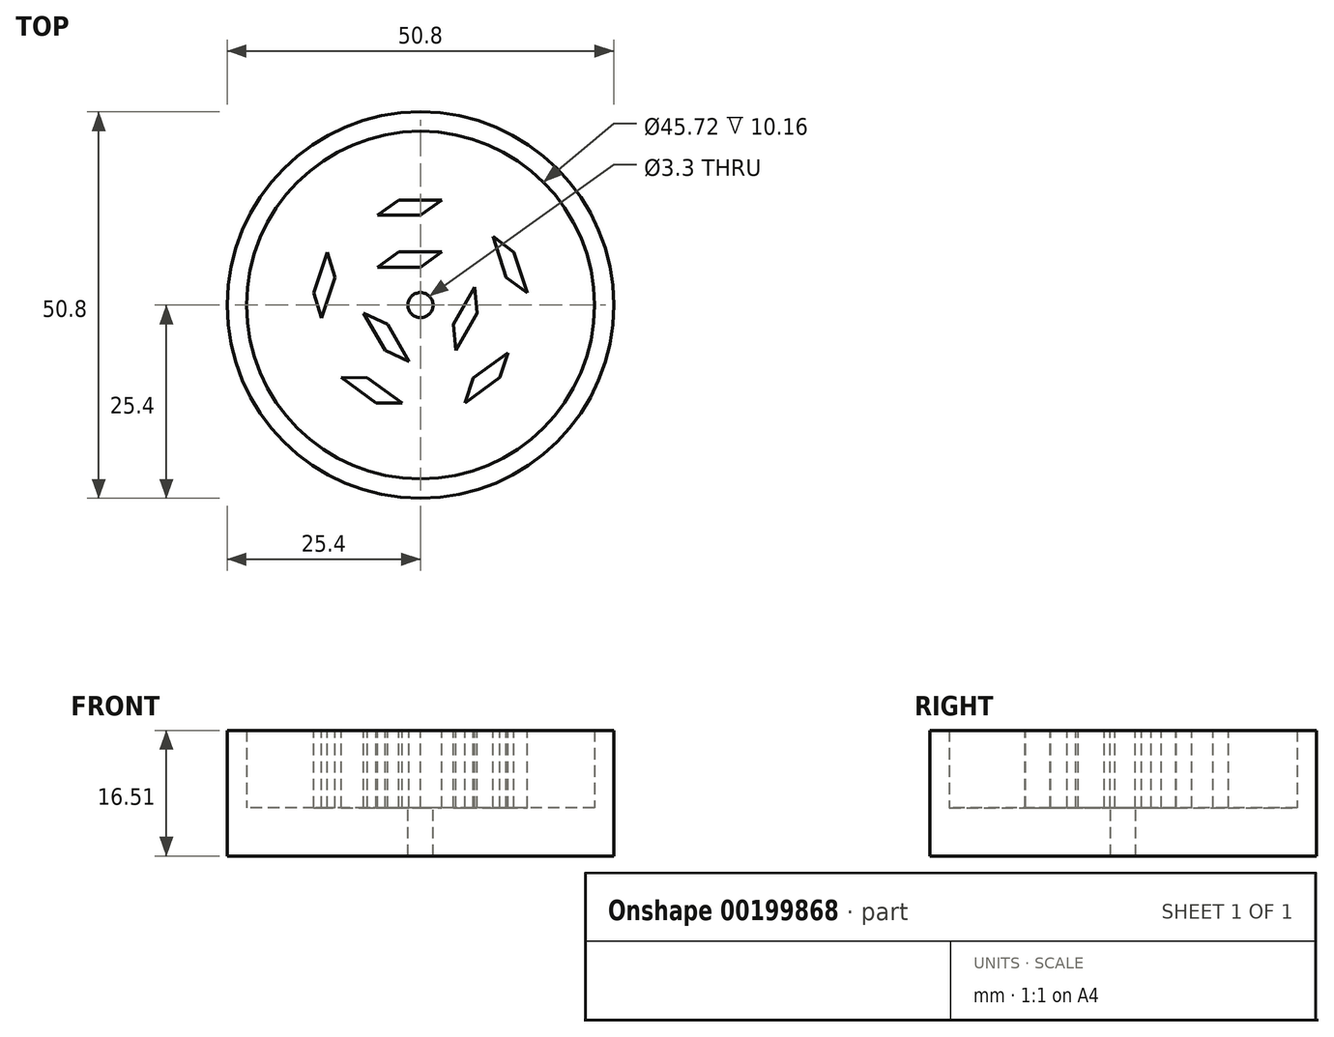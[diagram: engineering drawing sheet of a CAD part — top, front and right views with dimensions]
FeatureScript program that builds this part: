
annotation { "Feature Type Name" : "Feature", "Feature Type Description" : "" }
export const myFeature = defineFeature(function(context is Context, id is Id, definition is map)
    precondition{}
    {
        {
            var Q0;
            Q0=qCreatedBy(makeId("Top.planeOp"),FACE);
            var sketch = newSketch(context, id + "F0", { "sketchPlane" : qUnion([Q0])});
            skCircle(sketch, "E0", {"center": v(0, 0) * mm, "radius": 25.4 * mm});
            skSolve(sketch);
        }
        {
            var Q0;
            Q0=makeQuery(id+"F0.imprint","IMPRINT",FACE,{"disambiguationData":[TD([[makeQuery(id+"F0.imprint","IMPRINT",EDGE,{"derivedFrom":sQuery(id+"F0.wireOp",EDGE,"E0")}),1.0]])]});
            extrude(context, id + "F1", {"entities" : qUnion([Q0]), "depth" : 6.35 * mm});
        }
        {
            var Q0;
            Q0=makeQuery(id+"F1.opExtrude","CAP_FACE",FACE,{"disambiguationData":[OSD([sQuery(id+"F0.wireOp",EDGE,"E0")])],"isStart":false});
            var sketch = newSketch(context, id + "F2", { "sketchPlane" : qUnion([Q0])});
            skCircle(sketch, "E1", {"center": v(0, 0) * mm, "radius": 22.86 * mm});
            skSolve(sketch);
        }
        {
            var Q0;
            Q0=makeQuery(id+"F2.imprint","IMPRINT",FACE,{"disambiguationData":[TD([[makeQuery(id+"F2.imprint","IMPRINT",EDGE,{"derivedFrom":sQuery(id+"F2.wireOp",EDGE,"E1")}),1.0]])]});
            extrude(context, id + "F3", {"entities" : qUnion([Q0]), "operationType" : NewBodyOperationType.ADD, "depth" : 10.16 * mm});
        }
        {
            var Q0;
            Q0=makeQuery(id+"F3.opExtrude","CAP_FACE",FACE,{"disambiguationData":[OSD([sQuery(id+"F2.wireOp",EDGE,"E1")])],"isStart":false});
            var sketch = newSketch(context, id + "F4", { "sketchPlane" : qUnion([Q0])});
            skCircle(sketch, "E2", {"center": v(0, 0) * mm, "radius": 20.32 * mm});
            skCircle(sketch, "E3", {"center": v(0, 0) * mm, "radius": 1.65 * mm, "construction": true});
            skCircle(sketch, "E4.cCircle", {"center": v(0, 0) * mm, "radius": 1.53 * mm, "construction": true});
            skCircle(sketch, "E5", {"center": v(0, 0) * mm, "radius": 5 * mm, "construction": true});
            skCircle(sketch, "E6.0", {"center": v(0, 0) * mm, "radius": 7.53 * mm, "construction": true});
            skLineSegment(sketch, "E7", {"start": v(0, 5) * mm, "end": v(2.82, 6.98) * mm});
            skLineSegment(sketch, "E8", {"start": v(2.82, 6.98) * mm, "end": v(-2.82, 6.98) * mm});
            skLineSegment(sketch, "E9", {"start": v(-2.82, 6.98) * mm, "end": v(-5.64, 5) * mm});
            skLineSegment(sketch, "E10", {"start": v(-5.64, 5) * mm, "end": v(0, 5) * mm});
            skCircle(sketch, "E11", {"center": v(0, 0) * mm, "radius": 8.38 * mm, "construction": true});
            skCircle(sketch, "E12.0", {"center": v(0, 0) * mm, "radius": 10.92 * mm, "construction": true});
            skLineSegment(sketch, "E13", {"start": v(0, 8.56) * mm, "end": v(2.82, 10.55) * mm, "construction": true});
            skLineSegment(sketch, "E14", {"start": v(2.82, 10.55) * mm, "end": v(-2.82, 10.55) * mm, "construction": true});
            skLineSegment(sketch, "E15", {"start": v(-2.82, 10.55) * mm, "end": v(-5.64, 8.56) * mm, "construction": true});
            skLineSegment(sketch, "E16", {"start": v(-5.64, 8.56) * mm, "end": v(0, 8.56) * mm, "construction": true});
            skCircle(sketch, "E17", {"center": v(0, 0) * mm, "radius": 11.57 * mm, "construction": true});
            skCircle(sketch, "E18.0", {"center": v(0, 0) * mm, "radius": 14.1 * mm, "construction": true});
            skLineSegment(sketch, "E19", {"start": v(0, 11.83) * mm, "end": v(2.82, 13.82) * mm});
            skLineSegment(sketch, "E20", {"start": v(2.82, 13.82) * mm, "end": v(-2.82, 13.82) * mm});
            skLineSegment(sketch, "E21", {"start": v(-2.82, 13.82) * mm, "end": v(-5.64, 11.83) * mm});
            skLineSegment(sketch, "E22", {"start": v(-5.64, 11.83) * mm, "end": v(0, 11.83) * mm});
            skCircle(sketch, "E23", {"center": v(0, 0) * mm, "radius": 14.85 * mm});
            skCircle(sketch, "E24.0", {"center": v(0, 0) * mm, "radius": 17.39 * mm});
            skLineSegment(sketch, "E25", {"start": v(0, 15.17) * mm, "end": v(2.82, 17.16) * mm});
            skLineSegment(sketch, "E26", {"start": v(2.82, 17.16) * mm, "end": v(-2.82, 17.16) * mm});
            skLineSegment(sketch, "E27", {"start": v(-2.82, 17.16) * mm, "end": v(-5.64, 15.17) * mm, "construction": true});
            skLineSegment(sketch, "E28", {"start": v(-5.64, 15.17) * mm, "end": v(0, 15.17) * mm, "construction": true});
            skPoint(sketch, "E29", {"position": v(0, 17.16) * mm});
            skLineSegment(sketch, "E30", {"start": v(0, 0) * mm, "end": v(0, 26.22) * mm, "construction": true});
            skCircle(sketch, "E31.cCircle", {"center": v(0, 0) * mm, "radius": 1.7 * mm, "construction": true});
            skLineSegment(sketch, "E31.0", {"start": v(-2.95, -1.7) * mm, "end": v(0, 3.4) * mm, "construction": true});
            skLineSegment(sketch, "E31.1", {"start": v(0, 3.4) * mm, "end": v(2.95, -1.7) * mm, "construction": true});
            skLineSegment(sketch, "E31.2", {"start": v(2.95, -1.7) * mm, "end": v(-2.95, -1.7) * mm, "construction": true});
            skPoint(sketch, "E31.0.midPoint", {"position": v(-1.47, 0.85) * mm});
            skLineSegment(sketch, "E32.1.0", {"start": v(-11.86, 9.46) * mm, "end": v(-11.66, 12.9) * mm, "construction": true});
            skLineSegment(sketch, "E32.1.1", {"start": v(-15.37, 5.05) * mm, "end": v(-11.86, 9.46) * mm, "construction": true});
            skLineSegment(sketch, "E32.1.2", {"start": v(-15.17, 8.5) * mm, "end": v(-15.37, 5.05) * mm, "construction": true});
            skLineSegment(sketch, "E32.1.3", {"start": v(-11.66, 12.9) * mm, "end": v(-15.17, 8.5) * mm, "construction": true});
            skLineSegment(sketch, "E32.2.0", {"start": v(-14.79, -3.37) * mm, "end": v(-17.36, -1.07) * mm, "construction": true});
            skLineSegment(sketch, "E32.2.1", {"start": v(-13.53, -8.87) * mm, "end": v(-14.79, -3.37) * mm, "construction": true});
            skLineSegment(sketch, "E32.2.2", {"start": v(-16.1, -6.57) * mm, "end": v(-13.53, -8.87) * mm, "construction": true});
            skLineSegment(sketch, "E32.2.3", {"start": v(-17.36, -1.07) * mm, "end": v(-16.1, -6.57) * mm, "construction": true});
            skLineSegment(sketch, "E32.3.0", {"start": v(-6.58, -13.66) * mm, "end": v(-9.99, -14.24) * mm, "construction": true});
            skLineSegment(sketch, "E32.3.1", {"start": v(-1.5, -16.11) * mm, "end": v(-6.58, -13.66) * mm, "construction": true});
            skLineSegment(sketch, "E32.3.2", {"start": v(-4.9, -16.68) * mm, "end": v(-1.5, -16.11) * mm, "construction": true});
            skLineSegment(sketch, "E32.3.3", {"start": v(-9.99, -14.24) * mm, "end": v(-4.9, -16.68) * mm, "construction": true});
            skLineSegment(sketch, "E32.4.0", {"start": v(6.58, -13.66) * mm, "end": v(4.9, -16.68) * mm, "construction": true});
            skLineSegment(sketch, "E32.4.1", {"start": v(11.66, -11.22) * mm, "end": v(6.58, -13.66) * mm, "construction": true});
            skLineSegment(sketch, "E32.4.2", {"start": v(9.99, -14.24) * mm, "end": v(11.66, -11.22) * mm, "construction": true});
            skLineSegment(sketch, "E32.4.3", {"start": v(4.9, -16.68) * mm, "end": v(9.99, -14.24) * mm, "construction": true});
            skLineSegment(sketch, "E32.5.0", {"start": v(14.79, -3.37) * mm, "end": v(16.1, -6.57) * mm, "construction": true});
            skLineSegment(sketch, "E32.5.1", {"start": v(16.04, 2.12) * mm, "end": v(14.79, -3.37) * mm, "construction": true});
            skLineSegment(sketch, "E32.5.2", {"start": v(17.36, -1.07) * mm, "end": v(16.04, 2.12) * mm, "construction": true});
            skLineSegment(sketch, "E32.5.3", {"start": v(16.1, -6.57) * mm, "end": v(17.36, -1.07) * mm, "construction": true});
            skLineSegment(sketch, "E32.6.0", {"start": v(11.86, 9.46) * mm, "end": v(15.17, 8.5) * mm, "construction": true});
            skLineSegment(sketch, "E32.6.1", {"start": v(8.34, 13.87) * mm, "end": v(11.86, 9.46) * mm, "construction": true});
            skLineSegment(sketch, "E32.6.2", {"start": v(11.66, 12.9) * mm, "end": v(8.34, 13.87) * mm, "construction": true});
            skLineSegment(sketch, "E32.6.3", {"start": v(15.17, 8.5) * mm, "end": v(11.66, 12.9) * mm, "construction": true});
            skLineSegment(sketch, "E33.1.0", {"start": v(-8.56, 0) * mm, "end": v(-10.55, 2.82) * mm, "construction": true});
            skLineSegment(sketch, "E33.1.1", {"start": v(-10.55, 2.82) * mm, "end": v(-10.55, -2.82) * mm, "construction": true});
            skLineSegment(sketch, "E33.1.2", {"start": v(-8.56, -5.64) * mm, "end": v(-8.56, 0) * mm, "construction": true});
            skLineSegment(sketch, "E33.1.3", {"start": v(-10.55, -2.82) * mm, "end": v(-8.56, -5.64) * mm, "construction": true});
            skLineSegment(sketch, "E33.2.0", {"start": v(0, -8.56) * mm, "end": v(-2.82, -10.55) * mm, "construction": true});
            skLineSegment(sketch, "E33.2.1", {"start": v(-2.82, -10.55) * mm, "end": v(2.82, -10.55) * mm, "construction": true});
            skLineSegment(sketch, "E33.2.2", {"start": v(5.64, -8.56) * mm, "end": v(0, -8.56) * mm, "construction": true});
            skLineSegment(sketch, "E33.2.3", {"start": v(2.82, -10.55) * mm, "end": v(5.64, -8.56) * mm, "construction": true});
            skLineSegment(sketch, "E34.1.3.0", {"start": v(8.56, 0) * mm, "end": v(10.55, -2.82) * mm, "construction": true});
            skLineSegment(sketch, "E34.3.3.0", {"start": v(10.55, -2.82) * mm, "end": v(10.55, 2.82) * mm, "construction": true});
            skLineSegment(sketch, "E34.6.3.0", {"start": v(8.56, 5.64) * mm, "end": v(8.56, 0) * mm, "construction": true});
            skLineSegment(sketch, "E34.9.3.0", {"start": v(10.55, 2.82) * mm, "end": v(8.56, 5.64) * mm, "construction": true});
            skCircle(sketch, "E35", {"center": v(0, 0) * mm, "radius": 22.86 * mm});
            skLineSegment(sketch, "E36.1.0", {"start": v(-4.32, -2.5) * mm, "end": v(-7.46, -1.05) * mm});
            skLineSegment(sketch, "E36.1.1", {"start": v(-7.46, -1.05) * mm, "end": v(-4.64, -5.93) * mm});
            skLineSegment(sketch, "E36.1.2", {"start": v(-1.5, -7.38) * mm, "end": v(-4.32, -2.5) * mm});
            skLineSegment(sketch, "E36.1.3", {"start": v(-4.64, -5.93) * mm, "end": v(-1.5, -7.38) * mm});
            skLineSegment(sketch, "E36.2.0", {"start": v(4.32, -2.5) * mm, "end": v(4.64, -5.93) * mm});
            skLineSegment(sketch, "E36.2.1", {"start": v(4.64, -5.93) * mm, "end": v(7.46, -1.05) * mm});
            skLineSegment(sketch, "E36.2.2", {"start": v(7.14, 2.39) * mm, "end": v(4.32, -2.5) * mm});
            skLineSegment(sketch, "E36.2.3", {"start": v(7.46, -1.05) * mm, "end": v(7.14, 2.39) * mm});
            skLineSegment(sketch, "E37.1.0", {"start": v(-11.25, 3.66) * mm, "end": v(-12.27, 6.95) * mm});
            skLineSegment(sketch, "E37.1.1", {"start": v(-12.27, 6.95) * mm, "end": v(-14.02, 1.59) * mm});
            skLineSegment(sketch, "E37.1.2", {"start": v(-13, -1.7) * mm, "end": v(-11.25, 3.66) * mm});
            skLineSegment(sketch, "E37.1.3", {"start": v(-14.02, 1.59) * mm, "end": v(-13, -1.7) * mm});
            skLineSegment(sketch, "E37.2.0", {"start": v(-6.95, -9.57) * mm, "end": v(-10.4, -9.52) * mm});
            skLineSegment(sketch, "E37.2.1", {"start": v(-10.4, -9.52) * mm, "end": v(-5.84, -12.84) * mm});
            skLineSegment(sketch, "E37.2.2", {"start": v(-2.4, -12.89) * mm, "end": v(-6.95, -9.57) * mm});
            skLineSegment(sketch, "E37.2.3", {"start": v(-5.84, -12.84) * mm, "end": v(-2.4, -12.89) * mm});
            skLineSegment(sketch, "E37.3.0", {"start": v(6.95, -9.57) * mm, "end": v(5.84, -12.84) * mm});
            skLineSegment(sketch, "E37.3.1", {"start": v(5.84, -12.84) * mm, "end": v(10.4, -9.52) * mm});
            skLineSegment(sketch, "E37.3.2", {"start": v(11.52, -6.26) * mm, "end": v(6.95, -9.57) * mm});
            skLineSegment(sketch, "E37.3.3", {"start": v(10.4, -9.52) * mm, "end": v(11.52, -6.26) * mm});
            skLineSegment(sketch, "E37.4.0", {"start": v(11.25, 3.66) * mm, "end": v(14.02, 1.59) * mm});
            skLineSegment(sketch, "E37.4.1", {"start": v(14.02, 1.59) * mm, "end": v(12.27, 6.95) * mm});
            skLineSegment(sketch, "E37.4.2", {"start": v(9.5, 9.02) * mm, "end": v(11.25, 3.66) * mm});
            skLineSegment(sketch, "E37.4.3", {"start": v(12.27, 6.95) * mm, "end": v(9.5, 9.02) * mm});
            skSolve(sketch);
        }
        {
            var Q0;
            Q0=makeQuery(id+"F4.imprint","IMPRINT",FACE,{"disambiguationData":[TD([[makeQuery(id+"F4.imprint","IMPRINT",EDGE,{"derivedFrom":sQuery(id+"F4.wireOp",EDGE,"E2")}),-1.0]])]});
            var Q1;
            Q1=makeQuery(id+"F4.imprint","IMPRINT",FACE,{"disambiguationData":[TD([[makeQuery(id+"F4.imprint","IMPRINT",EDGE,{"derivedFrom":sQuery(id+"F4.wireOp",EDGE,"E23")}),-1.0]])]});
            var Q2;
            Q2=makeQuery(id+"F4.imprint","IMPRINT",FACE,{"disambiguationData":[TD([[makeQuery(id+"F4.imprint","IMPRINT",EDGE,{"derivedFrom":sQuery(id+"F4.wireOp",EDGE,"E7")}),-1.0]])]});
            var Q3;
            Q3=makeQuery(id+"F4.imprint","IMPRINT",FACE,{"disambiguationData":[TD([[makeQuery(id+"F4.imprint","IMPRINT",EDGE,{"derivedFrom":sQuery(id+"F4.wireOp",EDGE,"E2")}),1.0]])]});
            var Q4;
            {var subQ0=sQuery(id+"F4.wireOp",EDGE,"E26");Q4=makeQuery(id+"F4.imprint","IMPRINT",FACE,{"disambiguationData":[TD([[makeQuery(id+"F4.imprint","IMPRINT",EDGE,{"derivedFrom":subQ0}),-1.0]])]});}
            extrude(context, id + "F5", {"entities" : qUnion([Q0, Q1, Q2, Q3, Q4]), "operationType" : NewBodyOperationType.REMOVE, "oppositeDirection" : true, "depth" : 10.16 * mm});
        }
        {
            var Q0;
            Q0=makeQuery(id+"F5.boolean.opBoolean","MERGE",FACE,{"derivedFrom":[makeQuery(id+"F1.opExtrude","CAP_FACE",FACE,{"disambiguationData":[OSD([sQuery(id+"F0.wireOp",EDGE,"E0")])],"isStart":false}),makeQuery(id+"F5.opExtrude","CAP_FACE",FACE,{"disambiguationData":[OSD([sQuery(id+"F4.wireOp",EDGE,"E7"),sQuery(id+"F4.wireOp",EDGE,"E8"),sQuery(id+"F4.wireOp",EDGE,"E9"),sQuery(id+"F4.wireOp",EDGE,"E10"),sQuery(id+"F4.wireOp",EDGE,"E19"),sQuery(id+"F4.wireOp",EDGE,"E20"),sQuery(id+"F4.wireOp",EDGE,"E21"),sQuery(id+"F4.wireOp",EDGE,"E22"),sQuery(id+"F4.wireOp",EDGE,"E35"),sQuery(id+"F4.wireOp",EDGE,"E36.1.0"),sQuery(id+"F4.wireOp",EDGE,"E36.1.1"),sQuery(id+"F4.wireOp",EDGE,"E36.1.2"),sQuery(id+"F4.wireOp",EDGE,"E36.1.3"),sQuery(id+"F4.wireOp",EDGE,"E36.2.0"),sQuery(id+"F4.wireOp",EDGE,"E36.2.1"),sQuery(id+"F4.wireOp",EDGE,"E36.2.2"),sQuery(id+"F4.wireOp",EDGE,"E36.2.3"),sQuery(id+"F4.wireOp",EDGE,"E37.1.0"),sQuery(id+"F4.wireOp",EDGE,"E37.1.1"),sQuery(id+"F4.wireOp",EDGE,"E37.1.2"),sQuery(id+"F4.wireOp",EDGE,"E37.1.3"),sQuery(id+"F4.wireOp",EDGE,"E37.2.0"),sQuery(id+"F4.wireOp",EDGE,"E37.2.1"),sQuery(id+"F4.wireOp",EDGE,"E37.2.2"),sQuery(id+"F4.wireOp",EDGE,"E37.2.3"),sQuery(id+"F4.wireOp",EDGE,"E37.3.0"),sQuery(id+"F4.wireOp",EDGE,"E37.3.1"),sQuery(id+"F4.wireOp",EDGE,"E37.3.2"),sQuery(id+"F4.wireOp",EDGE,"E37.3.3"),sQuery(id+"F4.wireOp",EDGE,"E37.4.0"),sQuery(id+"F4.wireOp",EDGE,"E37.4.1"),sQuery(id+"F4.wireOp",EDGE,"E37.4.2"),sQuery(id+"F4.wireOp",EDGE,"E37.4.3")])],"isStart":false})]});
            var sketch = newSketch(context, id + "F6", { "sketchPlane" : qUnion([Q0])});
            skCircle(sketch, "E38.0", {"center": v(0, 0) * mm, "radius": 22.86 * mm});
            skCircle(sketch, "E39", {"center": v(0, 0) * mm, "radius": 25.4 * mm});
            skSolve(sketch);
        }
        {
            var Q0;
            Q0=makeQuery(id+"F6.imprint","IMPRINT",FACE,{"disambiguationData":[TD([[makeQuery(id+"F6.imprint","IMPRINT",EDGE,{"derivedFrom":sQuery(id+"F6.wireOp",EDGE,"E38.0")}),-1.0]])]});
            extrude(context, id + "F7", {"entities" : qUnion([Q0]), "operationType" : NewBodyOperationType.ADD, "depth" : 10.16 * mm});
        }
        {
            var Q0;
            Q0=makeQuery(id+"F5.boolean.opBoolean","MERGE",FACE,{"derivedFrom":[makeQuery(id+"F1.opExtrude","CAP_FACE",FACE,{"disambiguationData":[OSD([sQuery(id+"F0.wireOp",EDGE,"E0")])],"isStart":false}),makeQuery(id+"F5.opExtrude","CAP_FACE",FACE,{"disambiguationData":[OSD([sQuery(id+"F4.wireOp",EDGE,"E7"),sQuery(id+"F4.wireOp",EDGE,"E8"),sQuery(id+"F4.wireOp",EDGE,"E9"),sQuery(id+"F4.wireOp",EDGE,"E10"),sQuery(id+"F4.wireOp",EDGE,"E19"),sQuery(id+"F4.wireOp",EDGE,"E20"),sQuery(id+"F4.wireOp",EDGE,"E21"),sQuery(id+"F4.wireOp",EDGE,"E22"),sQuery(id+"F4.wireOp",EDGE,"E35"),sQuery(id+"F4.wireOp",EDGE,"E36.1.0"),sQuery(id+"F4.wireOp",EDGE,"E36.1.1"),sQuery(id+"F4.wireOp",EDGE,"E36.1.2"),sQuery(id+"F4.wireOp",EDGE,"E36.1.3"),sQuery(id+"F4.wireOp",EDGE,"E36.2.0"),sQuery(id+"F4.wireOp",EDGE,"E36.2.1"),sQuery(id+"F4.wireOp",EDGE,"E36.2.2"),sQuery(id+"F4.wireOp",EDGE,"E36.2.3"),sQuery(id+"F4.wireOp",EDGE,"E37.1.0"),sQuery(id+"F4.wireOp",EDGE,"E37.1.1"),sQuery(id+"F4.wireOp",EDGE,"E37.1.2"),sQuery(id+"F4.wireOp",EDGE,"E37.1.3"),sQuery(id+"F4.wireOp",EDGE,"E37.2.0"),sQuery(id+"F4.wireOp",EDGE,"E37.2.1"),sQuery(id+"F4.wireOp",EDGE,"E37.2.2"),sQuery(id+"F4.wireOp",EDGE,"E37.2.3"),sQuery(id+"F4.wireOp",EDGE,"E37.3.0"),sQuery(id+"F4.wireOp",EDGE,"E37.3.1"),sQuery(id+"F4.wireOp",EDGE,"E37.3.2"),sQuery(id+"F4.wireOp",EDGE,"E37.3.3"),sQuery(id+"F4.wireOp",EDGE,"E37.4.0"),sQuery(id+"F4.wireOp",EDGE,"E37.4.1"),sQuery(id+"F4.wireOp",EDGE,"E37.4.2"),sQuery(id+"F4.wireOp",EDGE,"E37.4.3")])],"isStart":false})]});
            var sketch = newSketch(context, id + "F8", { "sketchPlane" : qUnion([Q0])});
            skCircle(sketch, "E40", {"center": v(0, 0) * mm, "radius": 1.65 * mm});
            skSolve(sketch);
        }
        {
            var Q0;
            Q0=makeQuery(id+"F8.imprint","IMPRINT",FACE,{"disambiguationData":[TD([[makeQuery(id+"F8.imprint","IMPRINT",EDGE,{"derivedFrom":sQuery(id+"F8.wireOp",EDGE,"E40")}),1.0]])]});
            extrude(context, id + "F9", {"entities" : qUnion([Q0]), "operationType" : NewBodyOperationType.REMOVE, "endBound" : BoundingType.UP_TO_NEXT, "oppositeDirection" : true, "depth" : 25.4 * mm});
        }
    });
